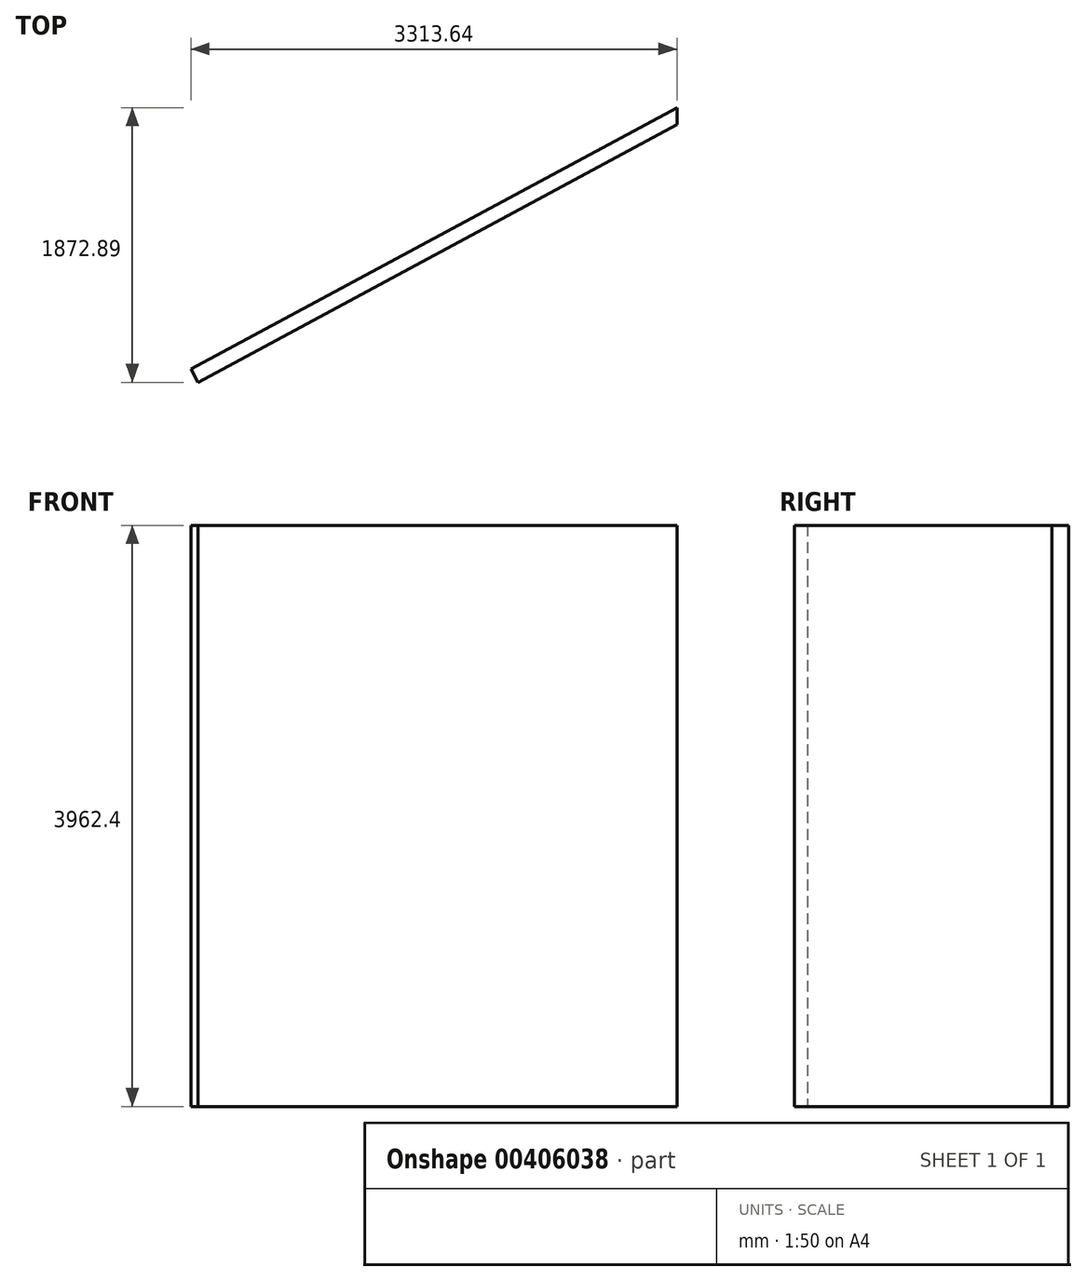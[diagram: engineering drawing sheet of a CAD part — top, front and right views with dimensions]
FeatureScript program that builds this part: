
annotation { "Feature Type Name" : "Feature", "Feature Type Description" : "" }
export const myFeature = defineFeature(function(context is Context, id is Id, definition is map)
    precondition{}
    {
        {
            var Q0;
            Q0=qCreatedBy(makeId("Top.planeOp"),FACE);
            var sketch = newSketch(context, id + "F0", { "sketchPlane" : qUnion([Q0])});
            skLineSegment(sketch, "E0", {"start": v(-415.32, -124.45) * mm, "end": v(-3680.8, -1881.96) * mm});
            skLineSegment(sketch, "E1", {"start": v(-3680.8, -1881.96) * mm, "end": v(-3728.96, -1792.5) * mm});
            skLineSegment(sketch, "E2", {"start": v(-3728.96, -1792.5) * mm, "end": v(-415.32, -9.07) * mm});
            skLineSegment(sketch, "E3", {"start": v(-415.32, -9.07) * mm, "end": v(-415.32, -124.45) * mm});
            skSolve(sketch);
        }
        {
            var Q0;
            Q0 = qSketchRegion(id + "F0", true);
            extrude(context, id + "F1", {"entities" : qUnion([Q0]), "depth" : 3962.4 * mm});
        }
    });
